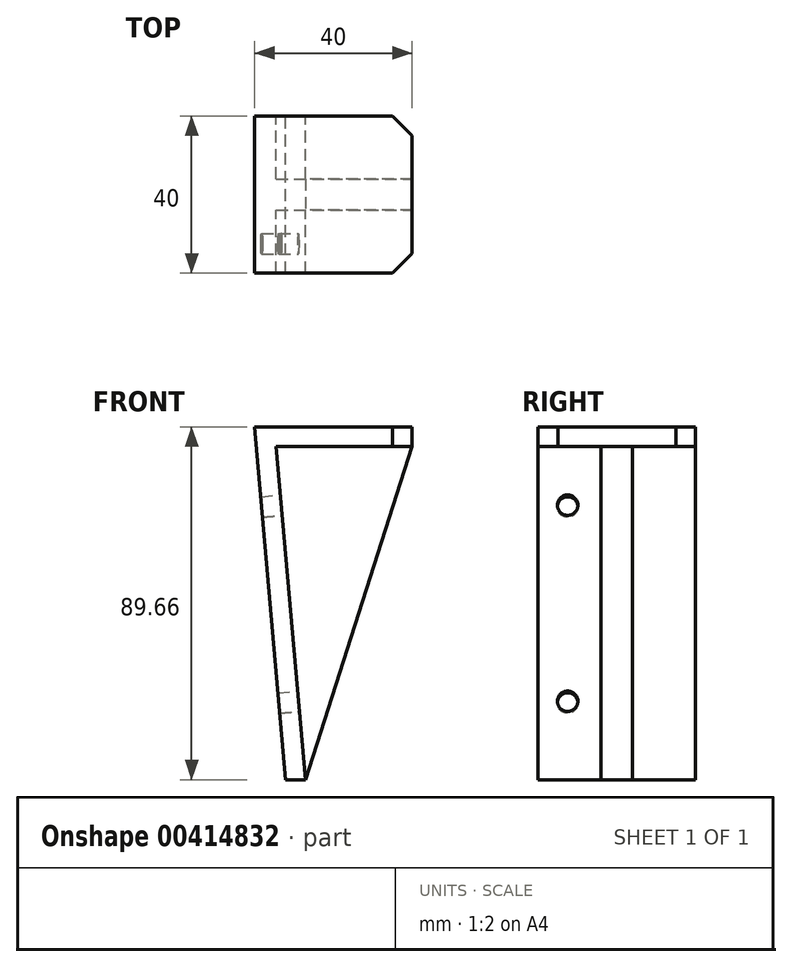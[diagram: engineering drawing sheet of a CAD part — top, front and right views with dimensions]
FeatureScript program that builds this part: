
annotation { "Feature Type Name" : "Feature", "Feature Type Description" : "" }
export const myFeature = defineFeature(function(context is Context, id is Id, definition is map)
    precondition{}
    {
        {
            var Q0;
            Q0=qCreatedBy(makeId("Front.planeOp"),FACE);
            var sketch = newSketch(context, id + "F0", { "sketchPlane" : qUnion([Q0])});
            skLineSegment(sketch, "E0", {"start": v(0, 0) * mm, "end": v(-7.84, 89.66) * mm});
            skLineSegment(sketch, "E1", {"start": v(-7.84, 89.66) * mm, "end": v(32.16, 89.66) * mm});
            skLineSegment(sketch, "E2", {"start": v(32.16, 89.66) * mm, "end": v(32.16, 84.66) * mm});
            skLineSegment(sketch, "E3", {"start": v(32.16, 84.66) * mm, "end": v(-2.39, 84.66) * mm});
            skLineSegment(sketch, "E4", {"start": v(-2.39, 84.66) * mm, "end": v(5.02, 0) * mm});
            skLineSegment(sketch, "E5", {"start": v(5.02, 0) * mm, "end": v(0, 0) * mm});
            skSolve(sketch);
        }
        {
            var Q0;
            Q0=makeQuery(id+"F0.imprint","IMPRINT",FACE,{"disambiguationData":[TD([[makeQuery(id+"F0.imprint","IMPRINT",EDGE,{"derivedFrom":sQuery(id+"F0.wireOp",EDGE,"E0")}),-1.0]])]});
            extrude(context, id + "F1", {"entities" : qUnion([Q0]), "endBound" : BoundingType.SYMMETRIC, "depth" : 40 * mm});
        }
        {
            var Q0;
            Q0=makeQuery(id+"F1.opExtrude","SWEPT_FACE",FACE,{"disambiguationData":[OSD([sQuery(id+"F0.wireOp",EDGE,"E2")])]});
            var sketch = newSketch(context, id + "F2", { "sketchPlane" : qUnion([Q0])});
            skLineSegment(sketch, "E6", {"start": v(0, -12.34) * mm, "end": v(0, 103.24) * mm, "construction": true});
            skPoint(sketch, "E6.endSnap0", {"position": v(0, 89.66) * mm});
            skLineSegment(sketch, "E7.bottom", {"start": v(-4, 0) * mm, "end": v(4, 0) * mm});
            skLineSegment(sketch, "E7.top", {"start": v(-4, 84.66) * mm, "end": v(4, 84.66) * mm});
            skLineSegment(sketch, "E7.left", {"start": v(-4, 0) * mm, "end": v(-4, 84.66) * mm});
            skLineSegment(sketch, "E7.right", {"start": v(4, 0) * mm, "end": v(4, 84.66) * mm});
            skSolve(sketch);
        }
        {
            var Q0;
            Q0=makeQuery(id+"F2.imprint","IMPRINT",FACE,{"disambiguationData":[TD([[makeQuery(id+"F2.imprint","IMPRINT",EDGE,{"derivedFrom":sQuery(id+"F2.wireOp",EDGE,"E7.bottom")}),1.0]])]});
            extrude(context, id + "F3", {"entities" : qUnion([Q0]), "operationType" : NewBodyOperationType.ADD, "endBound" : BoundingType.UP_TO_NEXT, "oppositeDirection" : true, "depth" : 25 * mm});
        }
        {
            var Q0;
            Q0=makeQuery(id+"F1.opExtrude","CAP_FACE",FACE,{"disambiguationData":[OSD([sQuery(id+"F0.wireOp",EDGE,"E0"),sQuery(id+"F0.wireOp",EDGE,"E1"),sQuery(id+"F0.wireOp",EDGE,"E2"),sQuery(id+"F0.wireOp",EDGE,"E3"),sQuery(id+"F0.wireOp",EDGE,"E4"),sQuery(id+"F0.wireOp",EDGE,"E5")])],"isStart":false});
            var sketch = newSketch(context, id + "F4", { "sketchPlane" : qUnion([Q0])});
            skLineSegment(sketch, "E8", {"start": v(5.02, 0) * mm, "end": v(32.16, 84.66) * mm});
            skLineSegment(sketch, "E9", {"start": v(32.16, 84.66) * mm, "end": v(32.16, 0) * mm});
            skLineSegment(sketch, "E10", {"start": v(32.16, 0) * mm, "end": v(5.02, 0) * mm});
            skSolve(sketch);
        }
        {
            var Q0;
            Q0=makeQuery(id+"F4.imprint","IMPRINT",FACE,{"disambiguationData":[TD([[makeQuery(id+"F4.imprint","IMPRINT",EDGE,{"derivedFrom":sQuery(id+"F4.wireOp",EDGE,"E8")}),-1.0]])]});
            extrude(context, id + "F5", {"entities" : qUnion([Q0]), "operationType" : NewBodyOperationType.REMOVE, "endBound" : BoundingType.THROUGH_ALL, "oppositeDirection" : true, "depth" : 25 * mm});
        }
        {
            var Q0;
            {var subQ1=sQuery(id+"F0.wireOp",EDGE,"E4");Q0=makeQuery(id+"F3.boolean.opBoolean","SPLIT",FACE,{"disambiguationData":[TD([makeQuery(id+"F3.opExtrude","SWEPT_FACE",FACE,{"disambiguationData":[OSD([sQuery(id+"F2.wireOp",EDGE,"E7.left")])]})])],"derivedFrom":makeQuery(id+"F1.opExtrude","SWEPT_FACE",FACE,{"disambiguationData":[OSD([subQ1])]})});}
            var sketch = newSketch(context, id + "F6", { "sketchPlane" : qUnion([Q0])});
            skLineSegment(sketch, "E11", {"start": v(0, 0) * mm, "end": v(0, 67.42) * mm, "construction": true});
            skCircle(sketch, "E12", {"center": v(-12.5, 69.56) * mm, "radius": 2.6 * mm});
            skCircle(sketch, "E13", {"center": v(-12.5, 19.56) * mm, "radius": 2.6 * mm});
            skCircle(sketch, "E14.MirrorC", {"center": v(12.5, 69.56) * mm, "radius": 2.6 * mm});
            skCircle(sketch, "E15.MirrorC", {"center": v(12.5, 19.56) * mm, "radius": 2.6 * mm});
            skSolve(sketch);
        }
        {
            var Q0;
            Q0=makeQuery(id+"F6.imprint","IMPRINT",FACE,{"disambiguationData":[TD([[makeQuery(id+"F6.imprint","IMPRINT",EDGE,{"derivedFrom":sQuery(id+"F6.wireOp",EDGE,"E14.MirrorC")}),-1.0]])]});
            var Q1;
            Q1=makeQuery(id+"F6.imprint","IMPRINT",FACE,{"disambiguationData":[TD([[makeQuery(id+"F6.imprint","IMPRINT",EDGE,{"derivedFrom":sQuery(id+"F6.wireOp",EDGE,"E15.MirrorC")}),-1.0]])]});
            var Q2;
            Q2=makeQuery(id+"F6.imprint","IMPRINT",FACE,{"disambiguationData":[TD([[makeQuery(id+"F6.imprint","IMPRINT",EDGE,{"derivedFrom":sQuery(id+"F6.wireOp",EDGE,"E12")}),1.0]])]});
            var Q3;
            Q3=makeQuery(id+"F6.imprint","IMPRINT",FACE,{"disambiguationData":[TD([[makeQuery(id+"F6.imprint","IMPRINT",EDGE,{"derivedFrom":sQuery(id+"F6.wireOp",EDGE,"E13")}),1.0]])]});
            extrude(context, id + "F7", {"entities" : qUnion([Q0, Q1, Q2, Q3]), "operationType" : NewBodyOperationType.REMOVE, "endBound" : BoundingType.THROUGH_ALL, "oppositeDirection" : true, "depth" : 25 * mm});
        }
        {
            var Q0;
            Q0=makeQuery(id+"F1.opExtrude","CAP_EDGE",EDGE,{"disambiguationData":[OSD([sQuery(id+"F0.wireOp",EDGE,"E2")])],"isStart":false});
            var Q1;
            Q1=makeQuery(id+"F1.opExtrude","CAP_EDGE",EDGE,{"disambiguationData":[OSD([sQuery(id+"F0.wireOp",EDGE,"E2")])],"isStart":true});
            chamfer(context, id + "F8", {"entities" : qUnion([Q0, Q1]), "width" : 5 * mm, "tangentPropagation" : true});
        }
    });
